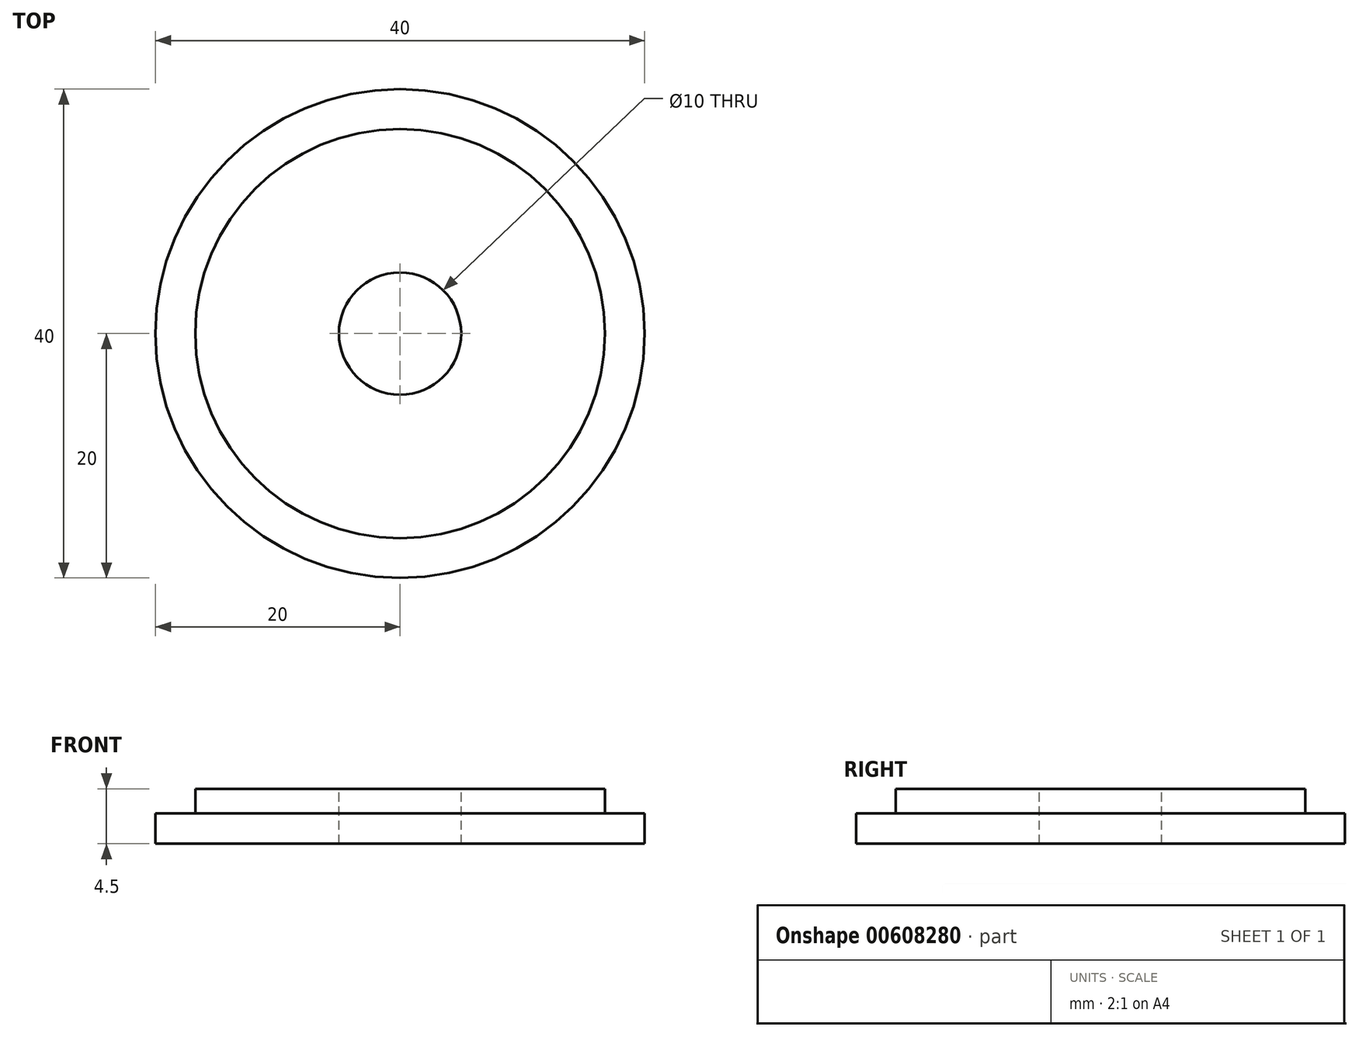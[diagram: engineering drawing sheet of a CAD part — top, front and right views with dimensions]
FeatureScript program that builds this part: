
annotation { "Feature Type Name" : "Feature", "Feature Type Description" : "" }
export const myFeature = defineFeature(function(context is Context, id is Id, definition is map)
    precondition{}
    {
        {
            var Q0;
            Q0=qCreatedBy(makeId("Top.planeOp"),FACE);
            var sketch = newSketch(context, id + "F0", { "sketchPlane" : qUnion([Q0])});
            skCircle(sketch, "E0", {"center": v(0, 0) * mm, "radius": 20 * mm});
            skSolve(sketch);
        }
        {
            var Q0;
            Q0=makeQuery(id+"F0.imprint","IMPRINT",FACE,{"disambiguationData":[TD([[makeQuery(id+"F0.imprint","IMPRINT",EDGE,{"derivedFrom":sQuery(id+"F0.wireOp",EDGE,"E0")}),1.0]])]});
            extrude(context, id + "F1", {"entities" : qUnion([Q0]), "depth" : 4.5 * mm, "offsetDistance" : 25 * mm});
        }
        {
            var Q0;
            Q0=makeQuery(id+"F1.opExtrude","CAP_FACE",FACE,{"disambiguationData":[OSD([sQuery(id+"F0.wireOp",EDGE,"E0")])],"isStart":false});
            var sketch = newSketch(context, id + "F2", { "sketchPlane" : qUnion([Q0])});
            skCircle(sketch, "E1", {"center": v(0, 0) * mm, "radius": 16.75 * mm});
            skCircle(sketch, "E2", {"center": v(0, 0) * mm, "radius": 42.41 * mm});
            skSolve(sketch);
        }
        {
            var Q0;
            Q0=makeQuery(id+"F2.imprint","IMPRINT",FACE,{"disambiguationData":[TD([[makeQuery(id+"F2.imprint","IMPRINT",EDGE,{"derivedFrom":sQuery(id+"F2.wireOp",EDGE,"E1")}),-1.0]])]});
            extrude(context, id + "F3", {"entities" : qUnion([Q0]), "operationType" : NewBodyOperationType.REMOVE, "oppositeDirection" : true, "depth" : 2 * mm, "offsetDistance" : 25 * mm});
        }
        {
            var Q0;
            Q0=makeQuery(id+"F1.opExtrude","CAP_FACE",FACE,{"disambiguationData":[OSD([sQuery(id+"F0.wireOp",EDGE,"E0")])],"isStart":false});
            var sketch = newSketch(context, id + "F4", { "sketchPlane" : qUnion([Q0])});
            skCircle(sketch, "E3", {"center": v(0, 0) * mm, "radius": 5 * mm});
            skSolve(sketch);
        }
        {
            var Q0;
            Q0 = qSketchRegion(id + "F4", true);
            extrude(context, id + "F5", {"entities" : qUnion([Q0]), "operationType" : NewBodyOperationType.REMOVE, "oppositeDirection" : true, "depth" : 6 * mm, "offsetDistance" : 25 * mm});
        }
    });
